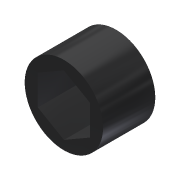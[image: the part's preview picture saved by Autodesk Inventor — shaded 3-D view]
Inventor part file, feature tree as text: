
AUTODESK INVENTOR PART (.ipt)
format: ipt  version: 2013 (Build 170138000, 138)  size: 81,920 bytes
history: native  units: in
note: dims shown in document units (in); Inventor stores cm internally (conversion verified against a paired STEP export)
features: extrude x1, sketch x1
ambient origin geometry x8: Origin, YZ Plane, XZ Plane, XY Plane, X Axis, Y Axis, Z Axis, Center Point
bodies: Solid1 (feature_tree)
feature tree (2):
  extrude  "Extrusion1"  Depth=0.5in
  sketch  "Sketch1"  dims[d0=0.75in d2=0.5in d3=0.5in d4=0.0in]
